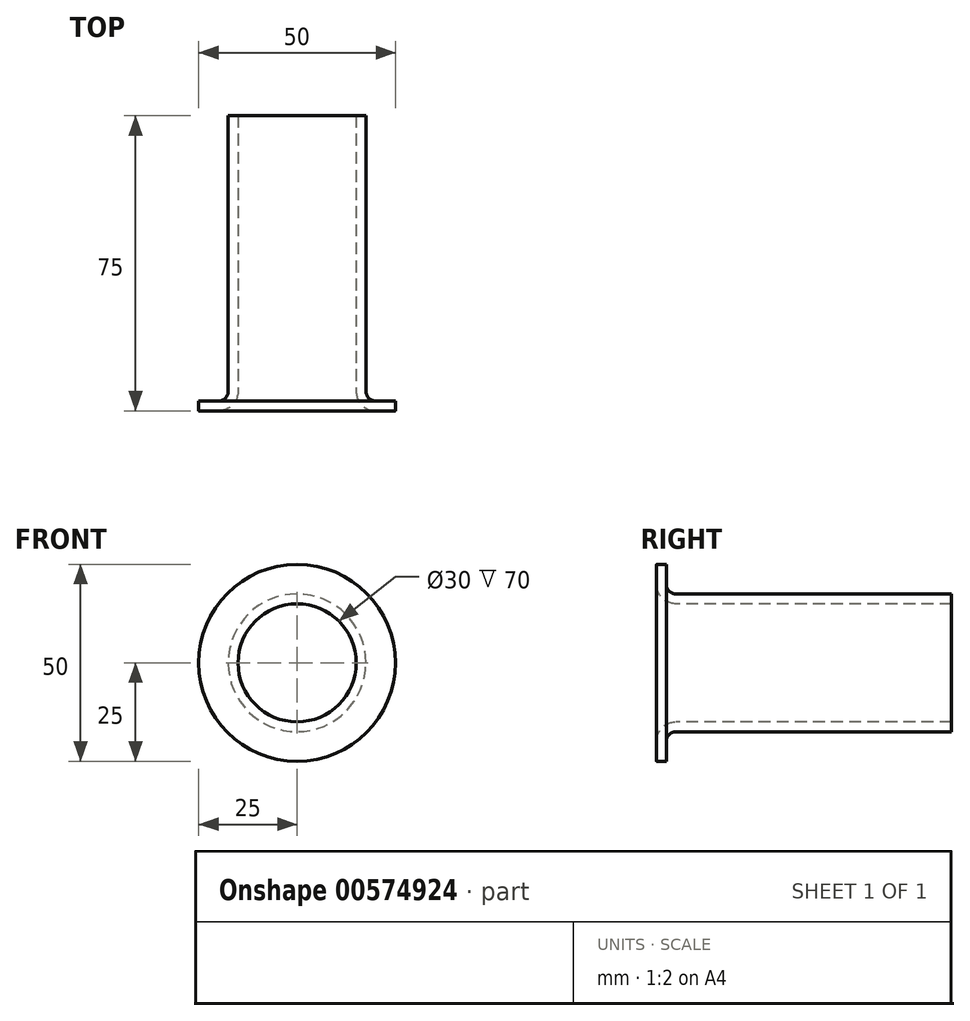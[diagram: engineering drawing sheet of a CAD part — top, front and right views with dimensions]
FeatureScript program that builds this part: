
annotation { "Feature Type Name" : "Feature", "Feature Type Description" : "" }
export const myFeature = defineFeature(function(context is Context, id is Id, definition is map)
    precondition{}
    {
        {
            var Q0;
            Q0=qCreatedBy(makeId("Right.planeOp"),FACE);
            var sketch = newSketch(context, id + "F0", { "sketchPlane" : qUnion([Q0])});
            skLineSegment(sketch, "E0", {"start": v(5, 15) * mm, "end": v(75, 15) * mm});
            skLineSegment(sketch, "E1", {"start": v(0, 25) * mm, "end": v(0, 20) * mm});
            skPoint(sketch, "E2.visualSharp", {"position": v(0, 15) * mm});
            skArc(sketch, "E2.filletArc", {"start": v(0, 20) * mm, "mid": v(1.46, 16.46) * mm, "end": v(5, 15) * mm});
            skLineSegment(sketch, "E3.0", {"start": v(5, 17.5) * mm, "end": v(75, 17.5) * mm});
            skLineSegment(sketch, "E3.1", {"start": v(2.5, 25) * mm, "end": v(2.5, 20) * mm});
            skPoint(sketch, "E4.visualSharp", {"position": v(2.5, 17.5) * mm});
            skArc(sketch, "E4.filletArc", {"start": v(2.5, 20) * mm, "mid": v(3.23, 18.23) * mm, "end": v(5, 17.5) * mm});
            skLineSegment(sketch, "E5", {"start": v(0, 25) * mm, "end": v(2.5, 25) * mm});
            skLineSegment(sketch, "E6", {"start": v(75, 17.5) * mm, "end": v(75, 15) * mm});
            skLineSegment(sketch, "E7", {"start": v(0, 0) * mm, "end": v(41.51, 0) * mm, "construction": true});
            skSolve(sketch);
        }
        {
            var Q0;
            Q0 = qSketchRegion(id + "F0", true);
            var Q1;
            Q1=sQuery(id+"F0.wireOp",EDGE,"E7");
            revolve(context, id + "F1", {"entities" : qUnion([Q0]), "axis" : qUnion([Q1]), "revolveType" : RevolveType.FULL});
        }
        {
            var Q0;
            Q0=makeQuery(id+"F1.opRevolve","SWEPT_EDGE",EDGE,{"disambiguationData":[OSD([sQuery(id+"F0.wireOp",EDGE,"E1"),sQuery(id+"F0.wireOp",EDGE,"E5")])]});
            fillet(context, id + "F2", {"entities" : qUnion([Q0]), "radius" : 0.1 * mm, "tangentPropagation" : true, "allowEdgeOverflow" : false});
        }
    });
